# Revit family: CGELED-80-WM_Lighting_Non-Hosted_R16
name_source: partatom
category: Lighting Fixtures
revit_build: Autodesk Revit 2016 (Build: 20151007_0715(x64)
units: mm (PartAtom-declared; Revit-internal decimal feet)

## family parameters
Always vertical = Yes
Cut with Voids When Loaded = No
Light Source = Yes
OmniClass Number = 23.80.70.00
OmniClass Title = Lighting
Part Type = Normal
Room Calculation Point = No
Round Connector Dimension = Use Diameter
Shared = No
Work Plane-Based = No

## types (7) — shared parameters
AS2293 Classification = C0=D80 C90=D80
Battery Type = Lithium Iron Phosphate
Charging Method = Intelligent Current Limited Constant Voltage
Color Filter = 16777215
Construction = Powder coated Metal Frame with Acrylic Diffuser
Dimensions (L x W x H) = 1305mm x 170mm x 560mm
Dimming Lamp Color Temperature Shift = <None>
Emergency Lumen Output = 443.7lm
Emit Shape Visible in Rendering = No
IP Rating = IP20
Manufacturer = Clevertronics
Mounting = Wall Mount, Single-Sided
Operating Mode = Maintained
Operating Temperature = 1˚C to 40˚C
Operating Voltage = 240V AC; 50Hz
Photometric Web File = CLIFE-PRO _IESA_E_LL22009B_20190729.IES
Power Consumption = 30 Watts
Power Consumption (Standby) = 23 Watts
Replacement Battery (EM) = 1550290 BATT:LP 6.4V 3.2Ah.200mm lead.Stick.Brkt
Replacement Battery (EXIT) = 1550230 BATT:LP 3.2V 6400mAh.200mm lead.Brkt.
Replacement Driver = 1330054 LED Driver - LC 38w 500-700mA, 20-54V
Replacement Lamp (EXIT) = 1100869 Lifelight Pro Head Assembly, Ld:280mm,Rnd,LT,Gen 2
Replacement lamp = 8002690 PCA:LED Strip Argonaut Stand & tray,1.2m
Tilt Angle = 90.00°
Viewing Distance = 80m
Weight = 21kg

## per-type parameters (varying)
| type | Applicable Standards | Battery | Description | Diffuser | Lamp | MIC Number | Model | Replacement Driver (EM) | Replacement Lifelight (EXIT) | Replacement Node (EM) | Replacement Node (EXIT) | Testing System |
| CGELED-80-WM-ZW-(RL/R/RR) |  | 3.2V 6400mAh, 6.4V 3200mAh | LP Premium Wall Mount Gigantor Exit, 80 metre viewing Distance | Running Man (must specify diffuser combination) | LED strip module, 4,000K natural white, 50,000h life [L70/B50 Ta 40°C], Ra>80 2 x 3W LED (Lifetime warranty on the Lamp head and loom Assembly) | AUA02110260001 | CGELED-80-WM-ZW-R | CCPLED-38V120C-CKIT-ZW LED Power Pack, 38V 120mA, LP, ZW, OWC | CLIFE-PRO-CKIT-ZW-NP LifelightPro,Control Only,530mm,ZW, NP, OWC | 8001460 PCA:Pwrln Node ZW Horizontal #CT10310-A6 | 8001450 PCA:Powerline Node ZW, #CT10310-A6 | Zoneworks computerised testing |
| CGELED-80-WM-R | AS/NZS3820, CISPR15, AS/NZS2293.3 | 3.2V 6400mAh (Exit), 6.4V 3200mAh (EM) | LP Premium Wall Mount Gigantor Exit, 80 metre Viewing Distance,
Enabled with Clevertest Plus | Running Man (must specify diffuser combination) | Exit: LED strip module, 4,000K natural white, Ra>80,
LED Lifetime: >100,000hrs (AS/NZS2293.3 LSL=39Y/00M), Ta 40°C
EM: 2 x 3W LED (Lifetime warranty on the Lamp head and loom Assembly) | AUA02310250001 | CGELED-80-WM-R
CGELED-80-WM-R
CGELED-80-WM-R | CCPLED-38V120C-CKIT LED Power Pack, 38V 120mA, LP | CLIFE-PRO-CKIT-NP LifelightPro,Control Only,Batten,LP, NP |  |  | Clevertest Plus Enabled (Not activated by default) |
| CGELED-80-WM-RL | AS/NZS3820, CISPR15, AS/NZS2293.3 | 3.2V 6400mAh (Exit), 6.4V 3200mAh (EM) | LP Premium Wall Mount Gigantor Exit, 80 metre Viewing Distance,
Enabled with Clevertest Plus
Enabled with Clevertest Plus | Running Man, Arrow Left (must specify diffuser combination) | Exit: LED strip module, 4,000K natural white, Ra>80,
LED Lifetime: >100,000hrs (AS/NZS2293.3 LSL=39Y/00M), Ta 40°C
EM: 2 x 3W LED (Lifetime warranty on the Lamp head and loom Assembly)
LED Lifetime: >100,000hrs (AS/NZS2293.3 LSL=39Y/00M), Ta 40°C
EM: 2 x 3W LED (Lifetime warranty on the Lamp head and loom Assembly) | AUA02310240001 | CGELED-80-WM-RL | CCPLED-38V120C-CKIT LED Power Pack, 38V 120mA, LP | CLIFE-PRO-CKIT-NP LifelightPro,Control Only,Batten,LP, NP |  |  | Clevertest Plus Enabled (Not activated by default) |
| CGELED-80-WM-RR | AS/NZS3820, CISPR15, AS/NZS2293.3 | 3.2V 6400mAh (Exit), 6.4V 3200mAh (EM) | LP Premium Wall Mount Gigantor Exit, 80 metre Viewing Distance,
Enabled with Clevertest Plus
Enabled with Clevertest Plus
Enabled with Clevertest Plus | Running Man, Arrow Right (must specify diffuser combination) | Exit: LED strip module, 4,000K natural white, Ra>80,
LED Lifetime: >100,000hrs (AS/NZS2293.3 LSL=39Y/00M), Ta 40°C
EM: 2 x 3W LED (Lifetime warranty on the Lamp head and loom Assembly) | AUA02310260001 | CGELED-80-WM-RR | CCPLED-38V120C-CKIT LED Power Pack, 38V 120mA, LP | CLIFE-PRO-CKIT-NP LifelightPro,Control Only,Batten,LP, NP |  |  | Clevertest Plus Enabled (Not activated by default) |
| CGELED-80-WM-R-BLK | AS/NZS3820, CISPR15, AS/NZS2293.3 | 3.2V 6400mAh (Exit), 6.4V 3200mAh (EM) | LP Premium Wall Mount Gigantor Exit, 80 metre Viewing Distance, Black, 
Enabled with Clevertest Plus | Running Man (must specify diffuser combination) | Exit: LED strip module, 4,000K natural white, Ra>80,
LED Lifetime: >100,000hrs (AS/NZS2293.3 LSL=39Y/00M), Ta 40°C
EM: 2 x 3W LED (Lifetime warranty on the Lamp head and loom Assembly) | AUA02310360001 | CGELED-80-WM-R-BLK | CCPLED-38V120C-CKIT LED Power Pack, 38V 120mA, LP | CLIFE-PRO-CKIT-NP LifelightPro,Control Only,Batten,LP, NP |  |  | Clevertest Plus Enabled (Not activated by default) |
| CGELED-80-WM-HV-(RL/R/RR) | AS/NZS3820, CISPR15, AS/NZS2293.3 | 3.2V 6400mAh (Exit), 6.4V 3200mAh (EM) | LP Premium Wall Mount Gigantor Exit, 80 metre viewing Distance, Hive | Running Man (must specify diffuser combination) | LED strip module, 4,000K natural white, 50,000h life [L70/B50 Ta 40°C], Ra>80
2 x 3W LED (Lifetime warranty on the Lamp head and loom Assembly) | AUA02810120001 | CGELED-80-WM-HV-R | CCPLED-38V120C-CKIT-HV LED Power Pack, 38V, 120mA, HV, LP | CLIFE-PRO-CKIT-HV-NP LifelightPro,Control Only,Batten,HV, LP | 8003192 PCA: RF Node CT10678-A12 Int Antenna Horizontal | 8003191 PCA: RF Node CT10678-A12 Int Antenna LLPro | Hive RF |
| CGELED-80-WM-HVG-R | AS/NZS3820, CISPR15, AS/NZS2293.3 | 3.2V 6400mAh (Exit), 6.4V 3200mAh (EM) | LP Premium Wall Mount Gigantor Exit, 80 metre viewing Distance, Hive 2.4G | Running Man (must specify diffuser combination) | LED strip module, 4,000K natural white, 50,000h life [L70/B50 Ta 40°C], Ra>80
2 x 3W LED (Lifetime warranty on the Lamp head and loom Assembly) | AUA02910120001 | CGELED-80-WM-HVG-R | CCPLED-38V120C-CKIT-HVG LED Power Pack, 38V, 120mA, HVG, LP | CLIFE-PRO-CKIT-HVG-NP LifelightPro,Control Only,HVG, LP | 8003560 PCA: V5 2.4GHz RF Node CT10816-A1 Int Ant | 8003570 PCA: V5 2.4GHz RF Node CT10816-A1 Int Ant Horiz | Hive RF 2.4G |

## geometry (parser evidence)
native form markers: Sweep x2
no freeform markers — native parametric forms only
